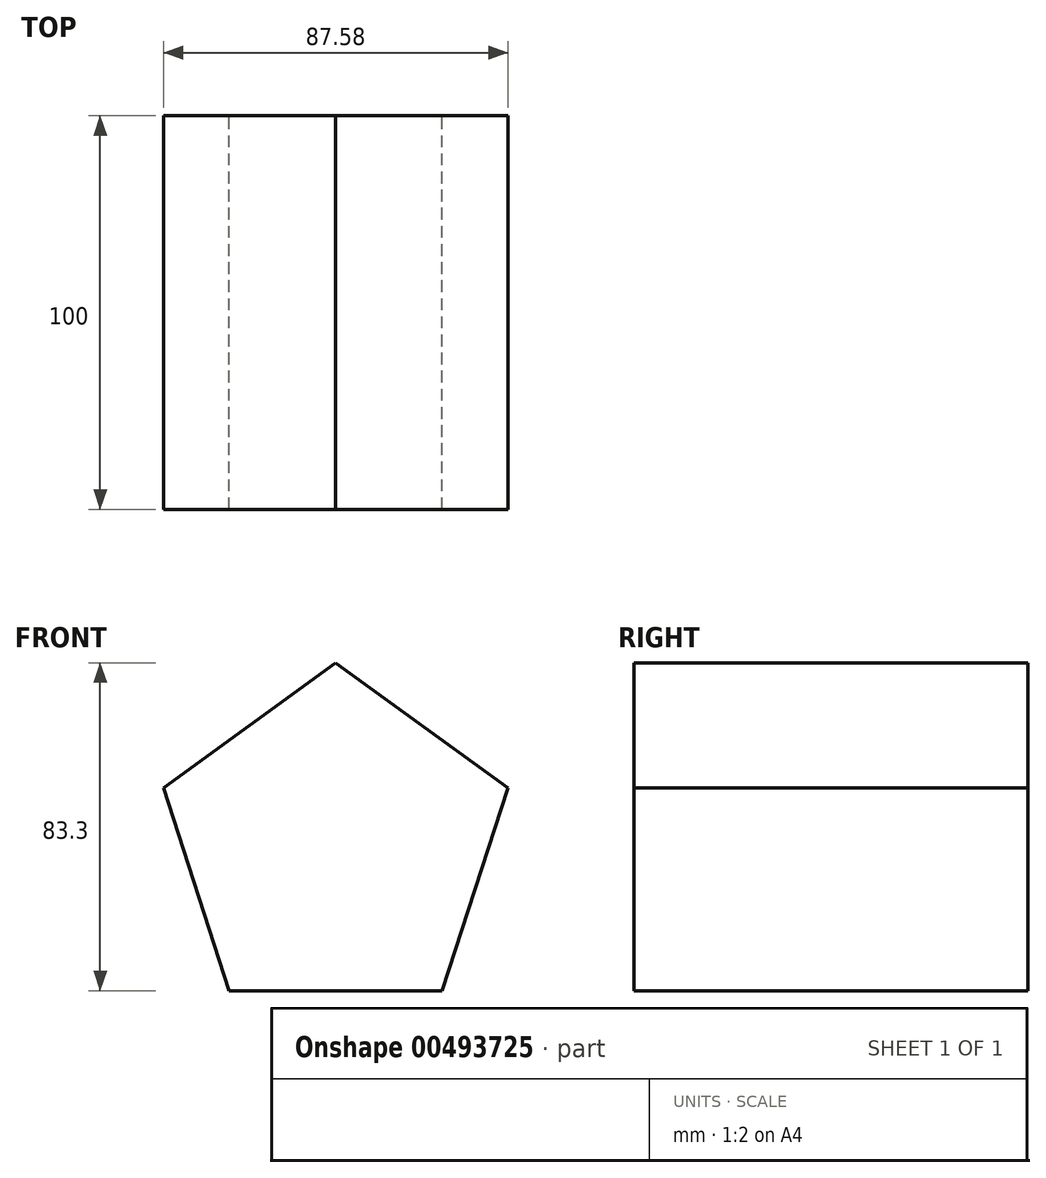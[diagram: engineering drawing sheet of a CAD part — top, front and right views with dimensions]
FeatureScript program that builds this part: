
annotation { "Feature Type Name" : "Feature", "Feature Type Description" : "" }
export const myFeature = defineFeature(function(context is Context, id is Id, definition is map)
    precondition{}
    {
        {
            var Q0;
            Q0=qCreatedBy(makeId("Front.planeOp"),FACE);
            var sketch = newSketch(context, id + "F0", { "sketchPlane" : qUnion([Q0])});
            skCircle(sketch, "E0.cCircle", {"center": v(0, 0) * mm, "radius": 46.05 * mm, "construction": true});
            skLineSegment(sketch, "E0.0", {"start": v(0, 46.05) * mm, "end": v(43.8, 14.23) * mm});
            skLineSegment(sketch, "E0.1", {"start": v(43.8, 14.23) * mm, "end": v(27.06, -37.25) * mm});
            skLineSegment(sketch, "E0.2", {"start": v(27.06, -37.25) * mm, "end": v(-27.06, -37.25) * mm});
            skLineSegment(sketch, "E0.3", {"start": v(-27.06, -37.25) * mm, "end": v(-43.8, 14.23) * mm});
            skLineSegment(sketch, "E0.4", {"start": v(-43.8, 14.23) * mm, "end": v(0, 46.05) * mm});
            skSolve(sketch);
        }
        {
            var Q0;
            Q0=makeQuery(id+"F0.imprint","IMPRINT",FACE,{"disambiguationData":[TD([[makeQuery(id+"F0.imprint","IMPRINT",EDGE,{"derivedFrom":sQuery(id+"F0.wireOp",EDGE,"E0.0")}),-1.0]])]});
            extrude(context, id + "F1", {"entities" : qUnion([Q0]), "endBound" : BoundingType.SYMMETRIC, "depth" : 100 * mm});
        }
    });
